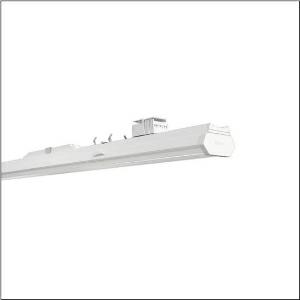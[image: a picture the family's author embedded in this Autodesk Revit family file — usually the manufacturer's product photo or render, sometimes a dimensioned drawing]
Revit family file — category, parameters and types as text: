
# Revit family: licross_r__21_protected_mo_52td11vn48xgd_36f3
name_source: partatom
category: Lighting Fixtures
units: mm (PartAtom-declared; Revit-internal decimal feet)

## family parameters
Cut with Voids When Loaded = No
Host = Face
Light Source = No
Part Type = Normal
Room Calculation Point = No
Round Connector Dimension = Use Diameter
Shared = No

## types (1)
- --- (1 x LED, 980 lm, 7 W, 4000K)
    Apparent Load = 7 VA
    CIE Flux Codes = 83 94 98 100 100
    Color Rendering = 80
    Color Temperature = 4000K
    Default Elevation = 1800 mm
    Description = Licross® 21 Protected MO, luminaire insert, of sheet steel, galvanised, coil coated, white, length: 1.500mm, width: 90mm, height: 103mm, LED rated luminous flux: 8.000lm, light colour: 840, control gear: DALI 2, CLO (for two DALI lines), with plug, 6-pole, with phase selection, mains connection: 220..240V, AC/DC, 0/50..60Hz, start of lifetime: 46W, end of service life: 52W, without changeover relay, for emergency light function, for central battery installations according to DIN EN 60598-2-22, halogen-free wiring, primary optical cover: cover, of PMMA, light emission: direct distribution, primary light characteristic: symmetric, protection rating (complete): IP54, insulation class (complete): insulation class I (protective earthing), certification: CE, ENEC, VDE, UKCA, protection symbol: D if used in an environment with non-conductive dust loads with corresponding accessories, impact resistance: IK06, permissible ambient temperature for indoor applications: -25..+50°C, standard: EN 60598-2-22, corresponds to IFS (International Featured Standards) requirements for safety and quality in the food industry, reducing of maximum allowable ambient temperature of 5°C with ceiling mounting, LABS conformity tested according to VDMA 24364:2018-05, packaging unit: 1 piece
    Height = 92 mm
    Lamp = 1 x LED
    Lamp Light Flux = 980 lm
    Lamp Power = 7 W
    Lamp count = 1
    Length = 1500 mm
    Luminous efficacy = 140 lm/W
    Manufacturer = Siteco
    ModVariant = No
    Model = 52TD11VN48XGD
    Mounting Place = Ceiling
    Mounting Type = Pendant
    Number of Poles = 1
    OnlyDefault = Yes
    Power Factor = 1
    Product Name = Licross® 21 Protected MO
    Product group = luminaire insert
    ProductGroupID = 902
    Protection Class = Protection class I
    Protection Degree = IP 54
    RLX_Detail_Level = 1
    RLX_Emergency_Light_Flux = 0 lm
    RLX_Emergency_Type = 0
    RLX_Emergency_Type_DB = No
    RlxData = <blob elided: 24549 chars, md5=fd731bac>
    Socket = socket
    Standby Power = 0 W
    System Light Flux = 980 lm
    System Power = 7 W
    Type Comments = : DC mode (central or group accumulator) initial emergency light level
    Type Image = l_1256148.jpg
    URL = http://relux.com
    VarID = @adj_082614
    Voltage = 0 V
    Weight = 0.00 kg
    Width = 88 mm

## geometry (parser evidence)
native form markers: Blend x4, Sweep x11
no freeform markers — native parametric forms only
